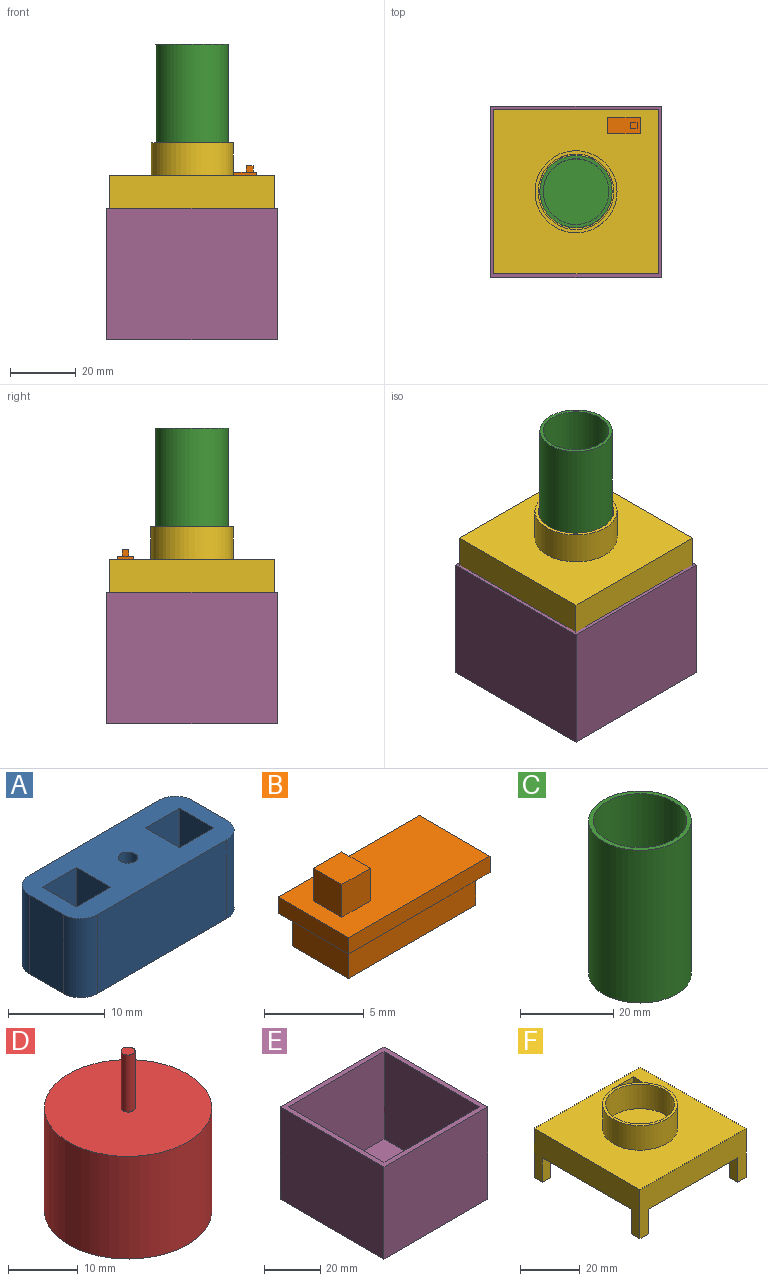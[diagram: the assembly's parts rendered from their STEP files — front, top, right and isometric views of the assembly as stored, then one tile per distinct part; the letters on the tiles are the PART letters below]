
ASSEMBLY  parts=6 mates=5
PART A: 21 faces, bbox 24x10x10 mm
  f0: plane 24x10mm, normal (0,0,1), area 181.5mm2, adj f1,f2,f3,f4,f6,f7,f8,f9
  f1: plane 19x10mm, normal (0,-1,0), area 190mm2, adj f0,f5,f17,f20
  f2: plane 10x5mm, normal (1,0,0), area 50mm2, adj f0,f5,f17,f18
  f3: plane 19x10mm, normal (0,1,0), area 190mm2, adj f0,f5,f18,f19
  f4: plane 10x5mm, normal (-1,0,0), area 50mm2, adj f0,f5,f19,f20
  f5: plane 24x10mm, normal (0,0,-1), area 231.5mm2, adj f1,f2,f3,f4,f16,f17,f18,f19
  f6: plane 9x5mm, normal (0,-1,0), area 45mm2, adj f0,f7,f9,f10
  f7: plane 9x5mm, normal (1,0,0), area 45mm2, adj f0,f6,f8,f10
  f8: plane 9x5mm, normal (0,1,0), area 45mm2, adj f0,f7,f9,f10
  f9: plane 9x5mm, normal (-1,0,0), area 45mm2, adj f0,f6,f8,f10
  f10: plane 5x5mm, normal (0,0,1), area 25mm2, adj f6,f7,f8,f9
  f11: plane 9x5mm, normal (0,-1,0), area 45mm2, adj f0,f12,f14,f15
  f12: plane 9x5mm, normal (1,0,0), area 45mm2, adj f0,f11,f13,f15
  f13: plane 9x5mm, normal (0,1,0), area 45mm2, adj f0,f12,f14,f15
  f14: plane 9x5mm, normal (-1,0,0), area 45mm2, adj f0,f11,f13,f15
  f15: plane 5x5mm, normal (0,0,1), area 25mm2, adj f11,f12,f13,f14
  f16: cylinder r=1mm len=10mm, axis (0,0,1), area 62.8mm2, adj f0,f5
  f17: cylinder r=2.5mm len=10mm, axis (0,0,1), area 39.3mm2, adj f0,f1,f2,f5
  f18: cylinder r=2.5mm len=10mm, axis (0,0,-1), area 39.3mm2, adj f0,f2,f3,f5
  f19: cylinder r=2.5mm len=10mm, axis (0,0,1), area 39.3mm2, adj f0,f3,f4,f5
  f20: cylinder r=2.5mm len=10mm, axis (0,0,-1), area 39.3mm2, adj f0,f1,f4,f5
PART B: 16 faces, bbox 10x5x5 mm
  f0: plane 10x5mm, normal (0,0,1), area 46mm2, adj f6,f7,f8,f9,f11,f12,f13,f14
  f1: plane 9x2mm, normal (0,-1,0), area 18mm2, adj f2,f4,f5,f10
  f2: plane 4x2mm, normal (1,0,0), area 8mm2, adj f1,f3,f5,f10
  f3: plane 9x2mm, normal (0,1,0), area 18mm2, adj f2,f4,f5,f10
  f4: plane 4x2mm, normal (-1,0,0), area 8mm2, adj f1,f3,f5,f10
  f5: plane 9x4mm, normal (0,0,-1), area 36mm2, adj f1,f2,f3,f4
  f6: plane 10x1mm, normal (0,-1,0), area 10mm2, adj f0,f7,f9,f10
  f7: plane 5x1mm, normal (1,0,0), area 5mm2, adj f0,f6,f8,f10
  f8: plane 10x1mm, normal (0,1,0), area 10mm2, adj f0,f7,f9,f10
  f9: plane 5x1mm, normal (-1,0,0), area 5mm2, adj f0,f6,f8,f10
  f10: plane 10x5mm, normal (0,0,-1), area 14mm2, adj f1,f2,f3,f4,f6,f7,f8,f9
  f11: plane 2x2mm, normal (0,-1,0), area 4mm2, adj f0,f12,f14,f15
  f12: plane 2x2mm, normal (1,0,0), area 4mm2, adj f0,f11,f13,f15
  f13: plane 2x2mm, normal (0,1,0), area 4mm2, adj f0,f12,f14,f15
  f14: plane 2x2mm, normal (-1,0,0), area 4mm2, adj f0,f11,f13,f15
  f15: plane 2x2mm, normal (0,0,1), area 4mm2, adj f11,f12,f13,f14
PART C: 5 faces, bbox 22x22x40 mm
  f0: cylinder r=11mm len=40mm, axis (0,0,-1), area 2764.6mm2, adj f1,f2
  f1: plane 22x22mm, normal (0,0,1), area 66mm2, adj f0,f4
  f2: plane 22x22mm, normal (0,0,-1), area 380.1mm2, adj f0
  f3: plane 20x20mm, normal (0,0,1), area 314.2mm2, adj f4
  f4: cylinder r=10mm len=38mm, axis (0,0,1), area 2387.6mm2, adj f1,f3
PART D: 5 faces, bbox 24x24x28 mm
  f0: cylinder r=12mm len=24mm, axis (0,0,-1), area 1357.2mm2, adj f1,f2
  f1: plane 24x24mm, normal (0,0,1), area 449.2mm2, adj f0,f3
  f2: plane 24x24mm, normal (0,0,-1), area 452.4mm2, adj f0
  f3: cylinder r=1mm len=10mm, axis (0,0,-1), area 62.8mm2, adj f1,f4
  f4: plane 2x2mm, normal (0,0,1), area 3.1mm2, adj f3
PART E: 11 faces, bbox 52x52x40 mm
  f0: plane 52x40mm, normal (0,-1,0), area 2080mm2, adj f1,f3,f4,f5
  f1: plane 52x40mm, normal (1,0,0), area 2080mm2, adj f0,f2,f4,f5
  f2: plane 52x40mm, normal (0,1,0), area 2080mm2, adj f1,f3,f4,f5
  f3: plane 52x40mm, normal (-1,0,0), area 2080mm2, adj f0,f2,f4,f5
  f4: plane 52x52mm, normal (0,0,1), area 400mm2, adj f0,f1,f2,f3,f7,f8,f9,f10
  f5: plane 52x52mm, normal (0,0,-1), area 2704mm2, adj f0,f1,f2,f3
  f6: plane 48x48mm, normal (0,0,1), area 2304mm2, adj f7,f8,f9,f10
  f7: plane 48x38mm, normal (-1,0,0), area 1824mm2, adj f4,f6,f8,f9
  f8: plane 48x38mm, normal (0,1,0), area 1824mm2, adj f4,f6,f7,f10
  f9: plane 48x38mm, normal (0,-1,0), area 1824mm2, adj f4,f6,f7,f10
  f10: plane 48x38mm, normal (1,0,0), area 1824mm2, adj f4,f6,f8,f9
PART F: 27 faces, bbox 50x50x30 mm
  f0: plane 50x20mm, normal (0,-1,0), area 580mm2, adj f1,f3,f4,f5,f11,f12,f20,f21
  f1: plane 50x20mm, normal (1,0,0), area 580mm2, adj f0,f2,f4,f5,f16,f18,f19,f21
  f2: plane 50x20mm, normal (0,1,0), area 580mm2, adj f1,f3,f4,f5,f14,f15,f17,f18
  f3: plane 50x20mm, normal (-1,0,0), area 580mm2, adj f0,f2,f4,f5,f10,f12,f13,f15
  f4: plane 50x50mm, normal (0,0,1), area 1959.1mm2, adj f0,f1,f2,f3,f6,f22,f23,f24
  f5: plane 50x50mm, normal (0,0,-1), area 2378.9mm2, adj f0,f1,f2,f3,f10,f11,f13,f14
  f6: cylinder r=12.5mm len=25mm, axis (0,0,-1), area 785.4mm2, adj f4,f7
  f7: plane 25x25mm, normal (0,0,1), area 75.4mm2, adj f6,f9
  f8: plane 23x23mm, normal (0,0,1), area 408.4mm2, adj f9,f26
  f9: cylinder r=11.5mm len=23mm, axis (0,0,1), area 722.6mm2, adj f7,f8
  f10: plane 10x4mm, normal (0,1,0), area 40mm2, adj f3,f5,f11,f12
  f11: plane 10x4mm, normal (1,0,0), area 40mm2, adj f0,f5,f10,f12
  f12: plane 4x4mm, normal (0,0,-1), area 16mm2, adj f0,f3,f10,f11
  f13: plane 10x4mm, normal (0,-1,0), area 40mm2, adj f3,f5,f14,f15
  f14: plane 10x4mm, normal (1,0,0), area 40mm2, adj f2,f5,f13,f15
  f15: plane 4x4mm, normal (0,0,-1), area 16mm2, adj f2,f3,f13,f14
  f16: plane 10x4mm, normal (0,-1,0), area 40mm2, adj f1,f5,f17,f18
  f17: plane 10x4mm, normal (-1,0,0), area 40mm2, adj f2,f5,f16,f18
  f18: plane 4x4mm, normal (0,0,-1), area 16mm2, adj f1,f2,f16,f17
  f19: plane 10x4mm, normal (0,1,0), area 40mm2, adj f1,f5,f20,f21
  f20: plane 10x4mm, normal (-1,0,0), area 40mm2, adj f0,f5,f19,f21
  f21: plane 4x4mm, normal (0,0,-1), area 16mm2, adj f0,f1,f19,f20
  f22: plane 10x5mm, normal (-1,0,0), area 50mm2, adj f4,f5,f23,f24
  f23: plane 10x10mm, normal (0,1,0), area 100mm2, adj f4,f5,f22,f25
  f24: plane 10x10mm, normal (0,-1,0), area 100mm2, adj f4,f5,f22,f25
  f25: plane 10x5mm, normal (1,0,0), area 50mm2, adj f4,f5,f23,f24
  f26: cylinder r=1.5mm len=10mm, axis (0,0,-1), area 94.2mm2, adj f5,f8
PLACE A t=(-15.19,-31.16,-43.84)mm
PLACE B rot(axis=(0,0,1),180deg) t=(-0.58,-10.96,-17.92)mm
PLACE C t=(-15.19,-31.16,-15.92)mm
PLACE D t=(-15.19,-31.16,-63.94)mm
PLACE E t=(-15.19,-31.16,-65.94)mm
PLACE F t=(-15.19,-31.16,-25.92)mm
MATE fastened B.f10 <-> F.f4  axis (0,0,-1) through (-5.58,-8.46,-15.92)mm
MATE fastened C.f0 <-> F.f9  axis (0,0,-1) through (-15.19,-31.16,-15.92)mm
MATE fastened D.f0 <-> E.f6  axis (0,0,-1) through (-15.19,-31.16,-63.94)mm
MATE slider A.f16 <-> D.f0  axis (0,0,-1) through (-15.19,-31.16,-43.84)mm
MATE slider F.f26 <-> D.f0  axis (0,0,-1) through (-15.19,-31.16,-25.92)mm
